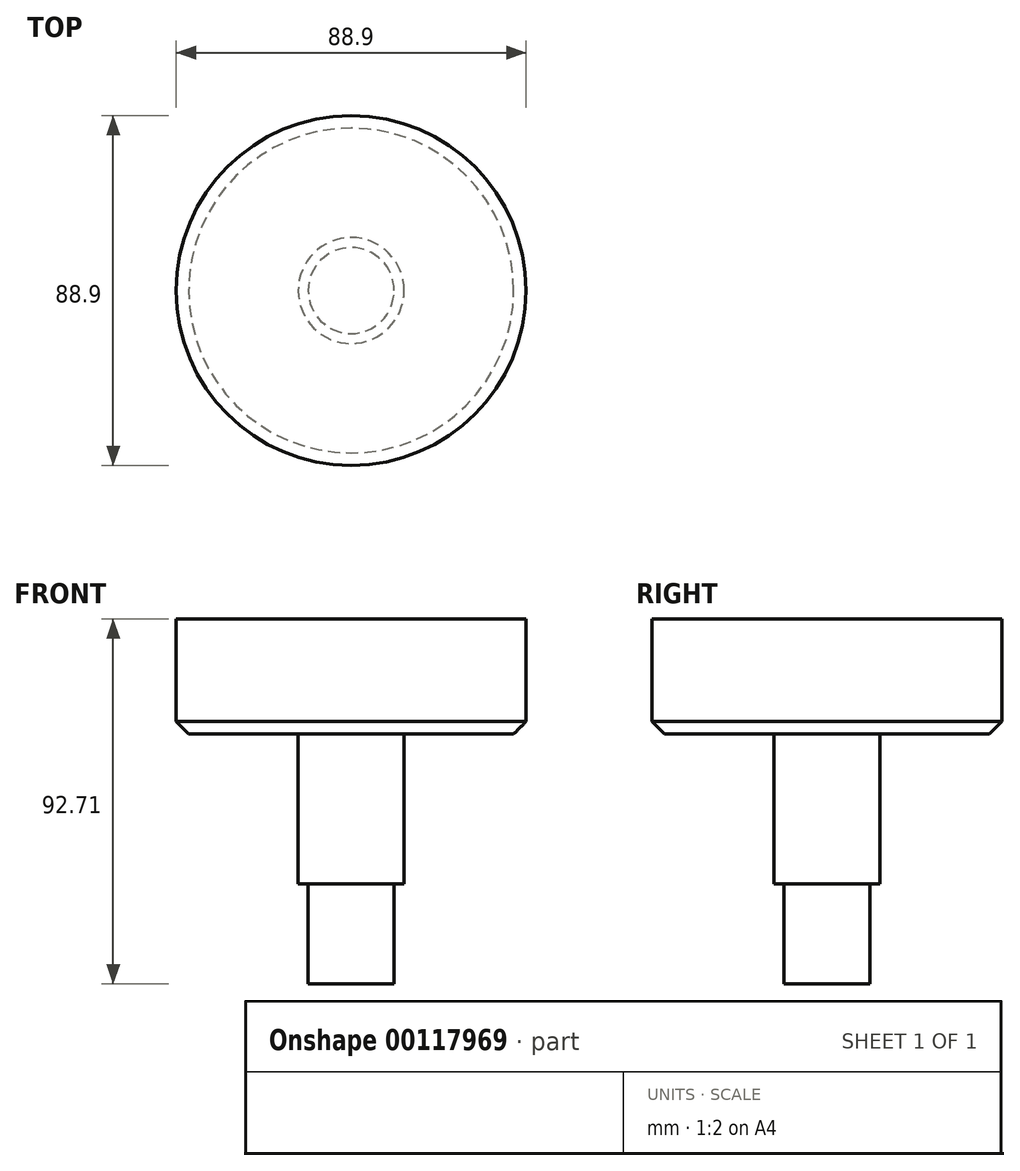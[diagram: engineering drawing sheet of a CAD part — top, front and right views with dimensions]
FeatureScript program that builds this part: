
annotation { "Feature Type Name" : "Feature", "Feature Type Description" : "" }
export const myFeature = defineFeature(function(context is Context, id is Id, definition is map)
    precondition{}
    {
        {
            var Q0;
            Q0=qCreatedBy(makeId("Top.planeOp"),FACE);
            var sketch = newSketch(context, id + "F0", { "sketchPlane" : qUnion([Q0])});
            skCircle(sketch, "E0", {"center": v(0, 0) * mm, "radius": 44.45 * mm});
            skSolve(sketch);
        }
        {
            var Q0;
            Q0 = qSketchRegion(id + "F0", true);
            extrude(context, id + "F1", {"entities" : qUnion([Q0]), "depth" : 29.2 * mm});
        }
        {
            var Q0;
            Q0=makeQuery(id+"F1.opExtrude","CAP_EDGE",EDGE,{"disambiguationData":[OSD([sQuery(id+"F0.wireOp",EDGE,"E0")])],"isStart":true});
            chamfer(context, id + "F2", {"entities" : qUnion([Q0]), "width" : 3.17 * mm, "tangentPropagation" : true});
        }
        {
            var Q0;
            Q0=makeQuery(id+"F1.opExtrude","CAP_FACE",FACE,{"disambiguationData":[OSD([sQuery(id+"F0.wireOp",EDGE,"E0")])],"isStart":true});
            var sketch = newSketch(context, id + "F3", { "sketchPlane" : qUnion([Q0])});
            skCircle(sketch, "E1", {"center": v(0, 0) * mm, "radius": 13.46 * mm});
            skSolve(sketch);
        }
        {
            var Q0;
            Q0 = qSketchRegion(id + "F3", true);
            extrude(context, id + "F4", {"entities" : qUnion([Q0]), "operationType" : NewBodyOperationType.ADD, "depth" : 38.1 * mm});
        }
        {
            var Q0;
            Q0=makeQuery(id+"F4.opExtrude","CAP_FACE",FACE,{"disambiguationData":[OSD([sQuery(id+"F3.wireOp",EDGE,"E1")])],"isStart":false});
            var sketch = newSketch(context, id + "F5", { "sketchPlane" : qUnion([Q0])});
            skCircle(sketch, "E2", {"center": v(0, 0) * mm, "radius": 10.92 * mm});
            skSolve(sketch);
        }
        {
            var Q0;
            Q0 = qSketchRegion(id + "F5", true);
            extrude(context, id + "F6", {"entities" : qUnion([Q0]), "operationType" : NewBodyOperationType.ADD, "depth" : 25.4 * mm});
        }
    });
